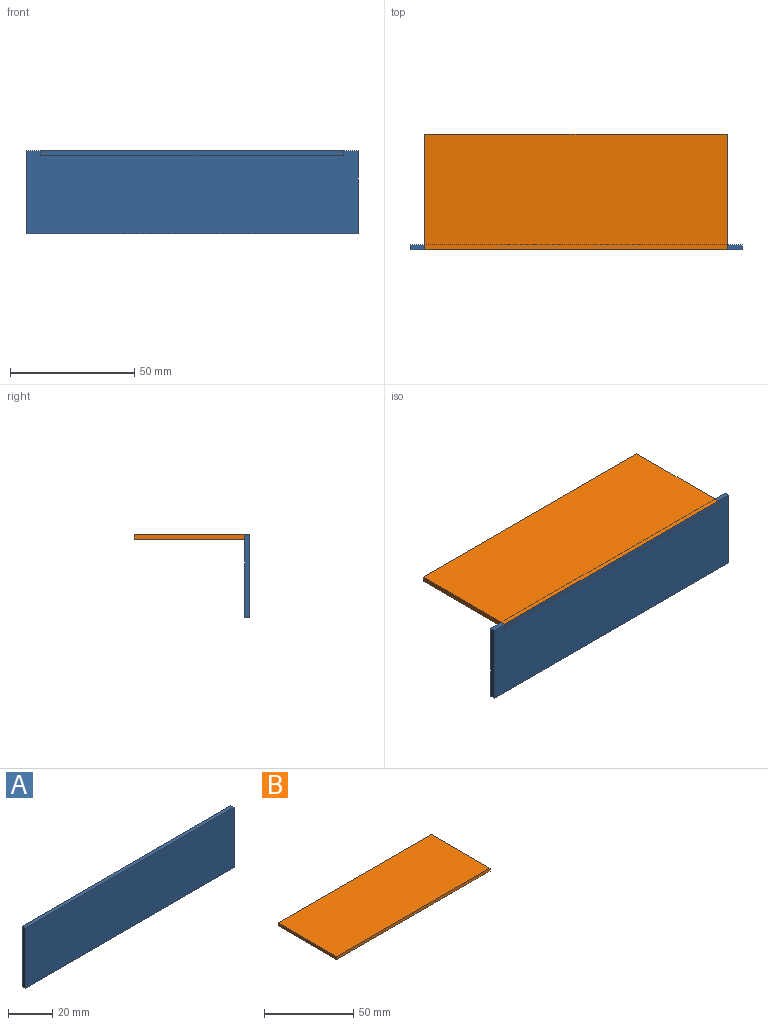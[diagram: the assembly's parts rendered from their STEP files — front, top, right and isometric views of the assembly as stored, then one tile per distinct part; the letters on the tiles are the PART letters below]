
ASSEMBLY  parts=2 mates=1
PART A: 6 faces, bbox 133.4x2x33.3 mm
  f0: plane 133.44x2mm, normal (0,0,-1), area 266.9mm2, adj f1,f3,f4,f5
  f1: plane 33.34x2mm, normal (1,0,0), area 66.7mm2, adj f0,f2,f4,f5
  f2: plane 133.44x2mm, normal (0,0,1), area 266.9mm2, adj f1,f3,f4,f5
  f3: plane 33.34x2mm, normal (-1,0,0), area 66.7mm2, adj f0,f2,f4,f5
  f4: plane 133.44x33.34mm, normal (0,-1,0), area 4449.3mm2, adj f0,f1,f2,f3
  f5: plane 133.44x33.34mm, normal (0,1,0), area 4449.3mm2, adj f0,f1,f2,f3
PART B: 6 faces, bbox 121.4x46.5x2 mm
  f0: plane 121.42x2mm, normal (0,-1,0), area 242.8mm2, adj f1,f3,f4,f5
  f1: plane 46.47x2mm, normal (1,0,0), area 92.9mm2, adj f0,f2,f4,f5
  f2: plane 121.42x2mm, normal (0,1,0), area 242.8mm2, adj f1,f3,f4,f5
  f3: plane 46.47x2mm, normal (-1,0,0), area 92.9mm2, adj f0,f2,f4,f5
  f4: plane 121.42x46.47mm, normal (0,0,1), area 5642.5mm2, adj f0,f1,f2,f3
  f5: plane 121.42x46.47mm, normal (0,0,-1), area 5642.5mm2, adj f0,f1,f2,f3
PLACE A t=(0,-25.2,-7.4)mm
PLACE B t=(0,-3.96,2.43)mm
MATE fastened B.f0 <-> A.f4  axis (0,-1,0) through (0,-27.2,3.43)mm
